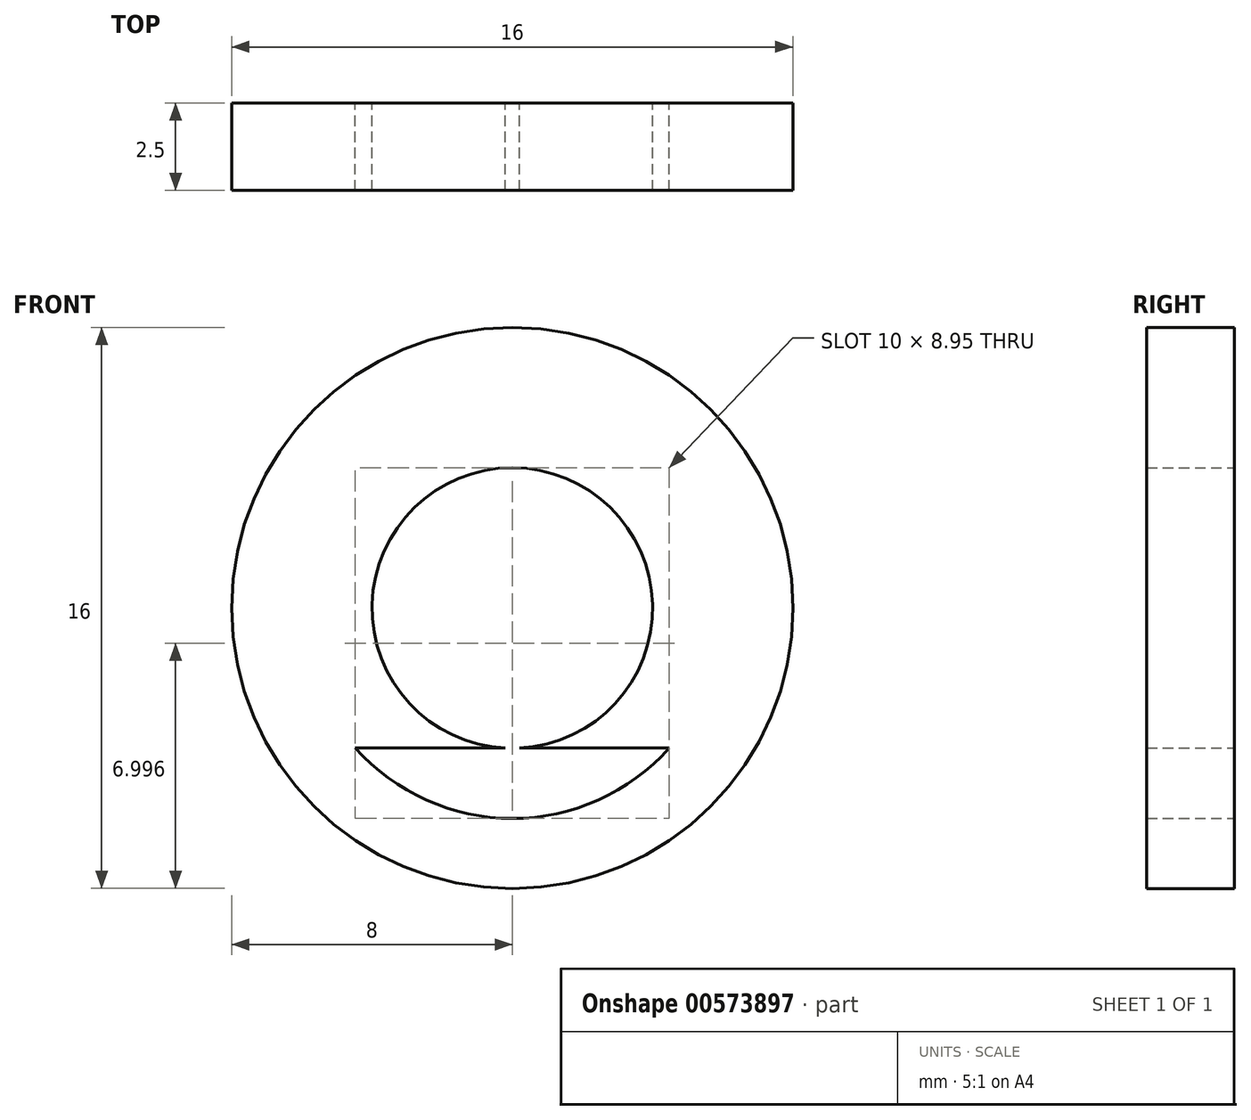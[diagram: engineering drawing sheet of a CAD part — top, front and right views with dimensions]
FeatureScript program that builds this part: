
annotation { "Feature Type Name" : "Feature", "Feature Type Description" : "" }
export const myFeature = defineFeature(function(context is Context, id is Id, definition is map)
    precondition{}
    {
        {
            var Q0;
            Q0=qCreatedBy(makeId("Front.planeOp"),FACE);
            var sketch = newSketch(context, id + "F0", { "sketchPlane" : qUnion([Q0])});
            skCircle(sketch, "E0", {"center": v(0, 0.69) * mm, "radius": 4 * mm});
            skCircle(sketch, "E1", {"center": v(0, 0.69) * mm, "radius": 6 * mm});
            skCircle(sketch, "E2", {"center": v(0, 0.69) * mm, "radius": 8 * mm});
            skCircle(sketch, "E3", {"center": v(0, 0.69) * mm, "radius": 13.37 * mm});
            skLineSegment(sketch, "E4", {"start": v(-6.93, -3.3) * mm, "end": v(6.93, -3.3) * mm});
            skSolve(sketch);
        }
        {
            var Q0;
            Q0=makeQuery(id+"F0.imprint","IMPRINT",FACE,{"disambiguationData":[TD([[makeQuery(id+"F0.imprint","IMPRINT",EDGE,{"derivedFrom":sQuery(id+"F0.wireOp",EDGE,"E2")}),1.0]])]});
            var Q1;
            {var subQ5=sQuery(id+"F0.wireOp",EDGE,"E0");var subQ7=makeQuery(id+"F0.imprint","IMPRINT",VERTEX,{"derivedFrom":subQ5});Q1=makeQuery(id+"F0.imprint","IMPRINT",FACE,{"disambiguationData":[TD([[makeQuery(id+"F0.imprint","IMPRINT",EDGE,{"disambiguationData":[TD([[subQ7,1.0]])],"derivedFrom":subQ5}),-1.0]])]});}
            var Q2;
            {var subQ0=sQuery(id+"F0.wireOp",EDGE,"b5cb84c5-cc38-40dd-89b2-e76e256370a7");var subQ1=sQuery(id+"F0.wireOp",EDGE,"E0");var subQ2=makeQuery(id+"F0.imprint","INTERSECT",VERTEX,{"disambiguationData":[OD(0.0)],"derivedFrom":[subQ1,subQ0]});Q2=makeQuery(id+"F0.imprint","IMPRINT",FACE,{"disambiguationData":[TD([[makeQuery(id+"F0.imprint","IMPRINT",EDGE,{"disambiguationData":[TD([[subQ2,-1.0]])],"derivedFrom":subQ1}),-1.0]])]});}
            extrude(context, id + "F1", {"entities" : qUnion([Q0, Q1, Q2]), "depth" : 2.5 * mm, "offsetDistance" : 25 * mm});
        }
    });
